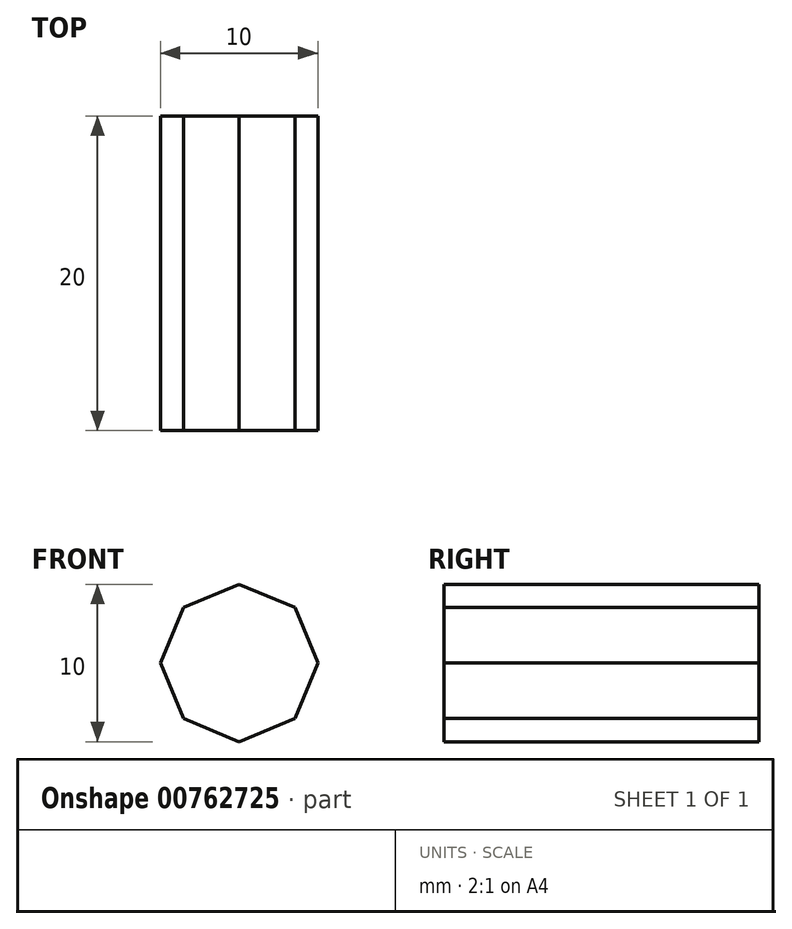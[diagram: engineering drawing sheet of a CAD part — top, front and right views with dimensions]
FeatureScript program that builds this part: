
annotation { "Feature Type Name" : "Feature", "Feature Type Description" : "" }
export const myFeature = defineFeature(function(context is Context, id is Id, definition is map)
    precondition{}
    {
        {
            var Q0;
            Q0=qCreatedBy(makeId("Front.planeOp"),FACE);
            var sketch = newSketch(context, id + "F0", { "sketchPlane" : qUnion([Q0])});
            skCircle(sketch, "E0.cCircle", {"center": v(0, 0) * mm, "radius": 5 * mm, "construction": true});
            skLineSegment(sketch, "E0.0", {"start": v(0, -5) * mm, "end": v(-3.54, -3.54) * mm});
            skLineSegment(sketch, "E0.1", {"start": v(-3.54, -3.54) * mm, "end": v(-5, 0) * mm});
            skLineSegment(sketch, "E0.2", {"start": v(-5, 0) * mm, "end": v(-3.54, 3.54) * mm});
            skLineSegment(sketch, "E0.3", {"start": v(-3.54, 3.54) * mm, "end": v(0, 5) * mm});
            skLineSegment(sketch, "E0.4", {"start": v(0, 5) * mm, "end": v(3.54, 3.54) * mm});
            skLineSegment(sketch, "E0.5", {"start": v(3.54, 3.54) * mm, "end": v(5, 0) * mm});
            skLineSegment(sketch, "E0.6", {"start": v(5, 0) * mm, "end": v(3.54, -3.54) * mm});
            skLineSegment(sketch, "E0.7", {"start": v(3.54, -3.54) * mm, "end": v(0, -5) * mm});
            skSolve(sketch);
        }
        {
            var Q0;
            Q0=makeQuery(id+"F0.imprint","IMPRINT",FACE,{"disambiguationData":[TD([[makeQuery(id+"F0.imprint","IMPRINT",EDGE,{"derivedFrom":sQuery(id+"F0.wireOp",EDGE,"E0.0")}),-1.0]])]});
            extrude(context, id + "F1", {"entities" : qUnion([Q0]), "endBound" : BoundingType.SYMMETRIC, "depth" : 20 * mm, "offsetDistance" : 25 * mm});
        }
    });
